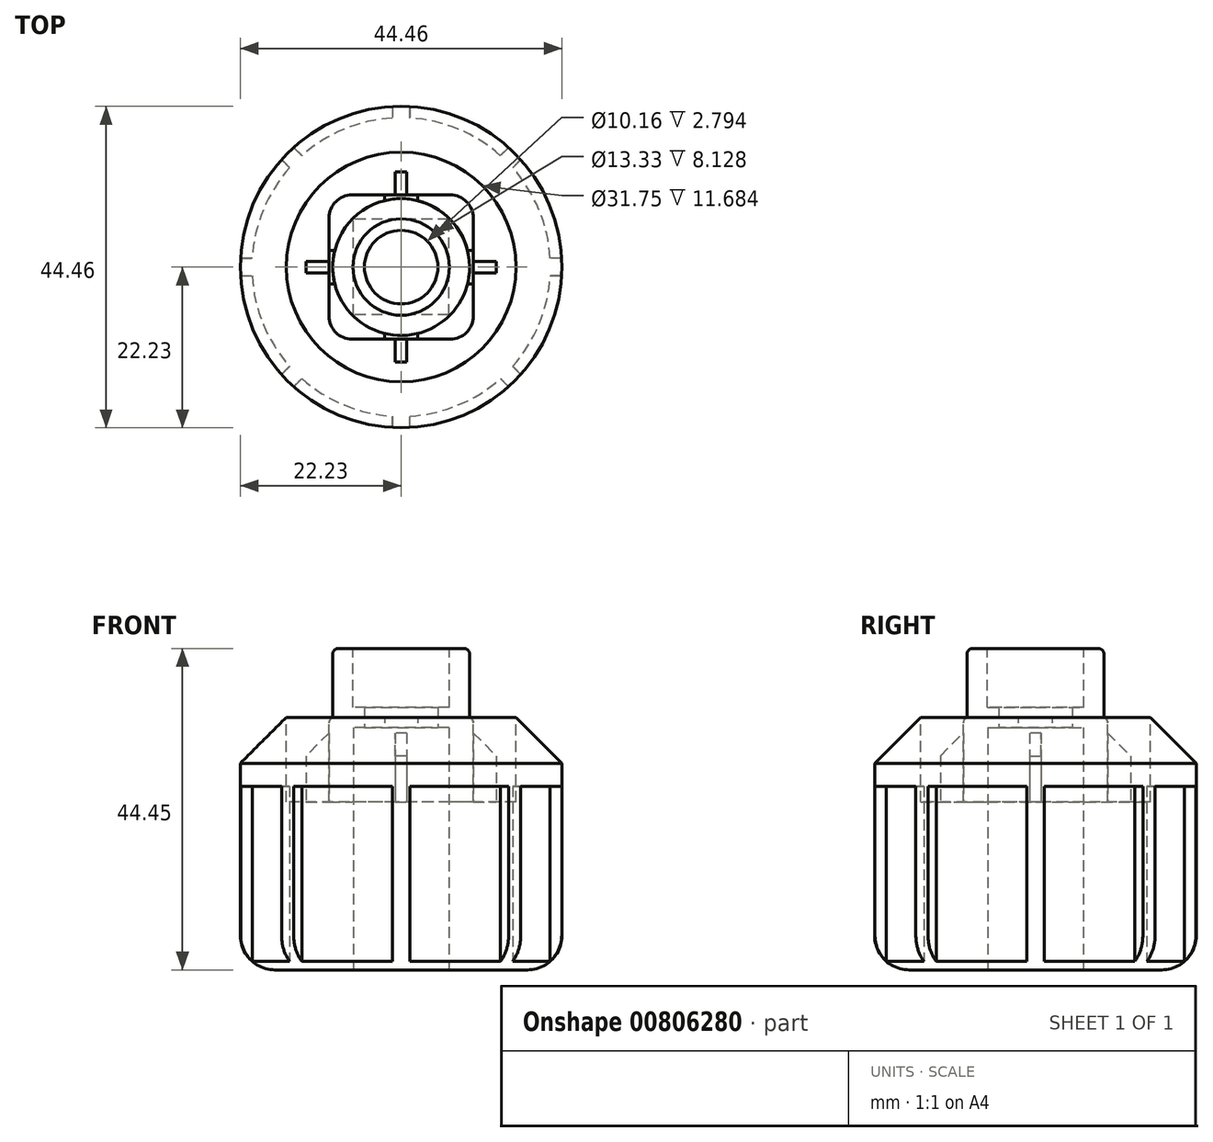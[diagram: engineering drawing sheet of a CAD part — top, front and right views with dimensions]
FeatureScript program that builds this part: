
annotation { "Feature Type Name" : "Feature", "Feature Type Description" : "" }
export const myFeature = defineFeature(function(context is Context, id is Id, definition is map)
    precondition{}
    {
        {
            var Q0;
            Q0=qCreatedBy(makeId("Top.planeOp"),FACE);
            var sketch = newSketch(context, id + "F0", { "sketchPlane" : qUnion([Q0])});
            skCircle(sketch, "E0", {"center": v(0, 0) * mm, "radius": 9.46 * mm});
            skCircle(sketch, "E1", {"center": v(0, 0) * mm, "radius": 5.08 * mm});
            skSolve(sketch);
        }
        {
            var Q0;
            Q0 = qSketchRegion(id + "F0", true);
            extrude(context, id + "F1", {"entities" : qUnion([Q0]), "depth" : 44.45 * mm, "offsetDistance" : 25.4 * mm});
        }
        {
            var Q0;
            Q0=makeQuery(id+"F1.opExtrude","CAP_FACE",FACE,{"disambiguationData":[OSD([sQuery(id+"F0.wireOp",EDGE,"E0"),sQuery(id+"F0.wireOp",EDGE,"E1")])],"isStart":true});
            var sketch = newSketch(context, id + "F2", { "sketchPlane" : qUnion([Q0])});
            skCircle(sketch, "E2", {"center": v(0, 0) * mm, "radius": 22.23 * mm});
            skCircle(sketch, "E3", {"center": v(0, 0) * mm, "radius": 5.08 * mm});
            skSolve(sketch);
        }
        {
            var Q0;
            Q0 = qSketchRegion(id + "F2", true);
            extrude(context, id + "F3", {"entities" : qUnion([Q0]), "operationType" : NewBodyOperationType.ADD, "oppositeDirection" : true, "depth" : 34.92 * mm, "offsetDistance" : 25.4 * mm});
        }
        {
            var Q0;
            Q0=makeQuery(id+"F1.opExtrude","CAP_FACE",FACE,{"disambiguationData":[OSD([sQuery(id+"F0.wireOp",EDGE,"E0"),sQuery(id+"F0.wireOp",EDGE,"E1")])],"isStart":false});
            var sketch = newSketch(context, id + "F4", { "sketchPlane" : qUnion([Q0])});
            skCircle(sketch, "E4", {"center": v(0, 0) * mm, "radius": 6.67 * mm});
            skSolve(sketch);
        }
        {
            var Q0;
            Q0 = qSketchRegion(id + "F4", true);
            extrude(context, id + "F5", {"entities" : qUnion([Q0]), "operationType" : NewBodyOperationType.REMOVE, "oppositeDirection" : true, "depth" : 8.13 * mm, "offsetDistance" : 25.4 * mm});
        }
        {
            var Q0;
            Q0=makeQuery(id+"F3.boolean.opBoolean","MERGE",FACE,{"derivedFrom":[makeQuery(id+"F1.opExtrude","CAP_FACE",FACE,{"disambiguationData":[OSD([sQuery(id+"F0.wireOp",EDGE,"E0"),sQuery(id+"F0.wireOp",EDGE,"E1")])],"isStart":true}),makeQuery(id+"F3.opExtrude","CAP_FACE",FACE,{"disambiguationData":[OSD([sQuery(id+"F2.wireOp",EDGE,"E2"),sQuery(id+"F2.wireOp",EDGE,"E3")])],"isStart":true})]});
            var sketch = newSketch(context, id + "F6", { "sketchPlane" : qUnion([Q0])});
            skLineSegment(sketch, "E5.bottom", {"start": v(6.6, 6.6) * mm, "end": v(-6.6, 6.6) * mm});
            skLineSegment(sketch, "E5.top", {"start": v(6.6, -6.6) * mm, "end": v(-6.6, -6.6) * mm});
            skLineSegment(sketch, "E5.left", {"start": v(6.6, 6.6) * mm, "end": v(6.6, -6.6) * mm});
            skLineSegment(sketch, "E5.right", {"start": v(-6.6, 6.6) * mm, "end": v(-6.6, -6.6) * mm});
            skPoint(sketch, "E5.middle", {"position": v(0, 0) * mm});
            skSolve(sketch);
        }
        {
            var Q0;
            Q0 = qSketchRegion(id + "F6", true);
            var Q1;
            Q1=makeQuery(id+"F1.opExtrude","CAP_FACE",FACE,{"disambiguationData":[OSD([sQuery(id+"F0.wireOp",EDGE,"E0"),sQuery(id+"F0.wireOp",EDGE,"E1")])],"isStart":false});
            extrude(context, id + "F7", {"entities" : qUnion([Q0, Q1]), "operationType" : NewBodyOperationType.REMOVE, "oppositeDirection" : true, "depth" : 33.53 * mm, "offsetDistance" : 25.4 * mm});
        }
        {
            var Q0;
            Q0=makeQuery(id+"F3.opExtrude","CAP_FACE",FACE,{"disambiguationData":[OSD([sQuery(id+"F2.wireOp",EDGE,"E2"),sQuery(id+"F2.wireOp",EDGE,"E3")])],"isStart":false});
            var sketch = newSketch(context, id + "F8", { "sketchPlane" : qUnion([Q0])});
            skLineSegment(sketch, "E6.bottom", {"start": v(6.8, 9.97) * mm, "end": v(-6.8, 9.97) * mm});
            skLineSegment(sketch, "E6.top", {"start": v(6.8, -9.97) * mm, "end": v(-6.8, -9.97) * mm});
            skLineSegment(sketch, "E6.left", {"start": v(9.97, 6.8) * mm, "end": v(9.97, -6.8) * mm});
            skLineSegment(sketch, "E6.right", {"start": v(-9.97, 6.8) * mm, "end": v(-9.97, -6.8) * mm});
            skPoint(sketch, "E6.middle", {"position": v(0, 0) * mm});
            skCircle(sketch, "E7", {"center": v(0, 0) * mm, "radius": 15.88 * mm});
            skPoint(sketch, "E8.visualSharp", {"position": v(-9.97, 9.97) * mm});
            skArc(sketch, "E8.filletArc", {"start": v(-6.8, 9.97) * mm, "mid": v(-9.04, 9.04) * mm, "end": v(-9.97, 6.8) * mm});
            skPoint(sketch, "E9.visualSharp", {"position": v(9.97, 9.97) * mm});
            skArc(sketch, "E9.filletArc", {"start": v(9.97, 6.8) * mm, "mid": v(9.04, 9.04) * mm, "end": v(6.8, 9.97) * mm});
            skPoint(sketch, "E10.visualSharp", {"position": v(9.97, -9.97) * mm});
            skArc(sketch, "E10.filletArc", {"start": v(6.8, -9.97) * mm, "mid": v(9.04, -9.04) * mm, "end": v(9.97, -6.8) * mm});
            skPoint(sketch, "E11.visualSharp", {"position": v(-9.97, -9.97) * mm});
            skArc(sketch, "E11.filletArc", {"start": v(-9.97, -6.8) * mm, "mid": v(-9.04, -9.04) * mm, "end": v(-6.8, -9.97) * mm});
            skSolve(sketch);
        }
        {
            var Q0;
            Q0 = qSketchRegion(id + "F8", true);
            extrude(context, id + "F9", {"entities" : qUnion([Q0]), "operationType" : NewBodyOperationType.REMOVE, "oppositeDirection" : true, "depth" : 11.68 * mm, "offsetDistance" : 25.4 * mm});
        }
        {
            var Q0;
            Q0=makeQuery(id+"F9.boolean.opBoolean","COPY",FACE,{"derivedFrom":makeQuery(id+"F9.opExtrude","CAP_FACE",FACE,{"disambiguationData":[OSD([sQuery(id+"F8.wireOp",EDGE,"E6.bottom"),sQuery(id+"F8.wireOp",EDGE,"E6.top"),sQuery(id+"F8.wireOp",EDGE,"E6.left"),sQuery(id+"F8.wireOp",EDGE,"E6.right"),sQuery(id+"F8.wireOp",EDGE,"E7"),sQuery(id+"F8.wireOp",EDGE,"E8.filletArc"),sQuery(id+"F8.wireOp",EDGE,"E9.filletArc"),sQuery(id+"F8.wireOp",EDGE,"E10.filletArc"),sQuery(id+"F8.wireOp",EDGE,"E11.filletArc")])],"isStart":false})});
            var sketch = newSketch(context, id + "F10", { "sketchPlane" : qUnion([Q0])});
            skLineSegment(sketch, "E12", {"start": v(-0.8, -9.97) * mm, "end": v(-0.8, -13.14) * mm});
            skLineSegment(sketch, "E13", {"start": v(-0.8, -13.14) * mm, "end": v(0.8, -13.14) * mm});
            skLineSegment(sketch, "E14", {"start": v(0.8, -13.14) * mm, "end": v(0.8, -9.97) * mm});
            skLineSegment(sketch, "E15", {"start": v(0.8, -9.97) * mm, "end": v(-0.8, -9.97) * mm});
            skLineSegment(sketch, "E16", {"start": v(0, -13.14) * mm, "end": v(0, -9.97) * mm, "construction": true});
            skLineSegment(sketch, "E17.1.0", {"start": v(-13.14, -0.8) * mm, "end": v(-9.97, -0.8) * mm});
            skLineSegment(sketch, "E17.1.1", {"start": v(-13.14, 0.8) * mm, "end": v(-13.14, -0.8) * mm});
            skLineSegment(sketch, "E17.1.2", {"start": v(-9.97, 0.8) * mm, "end": v(-13.14, 0.8) * mm});
            skLineSegment(sketch, "E17.1.3", {"start": v(-9.97, -0.8) * mm, "end": v(-9.97, 0.8) * mm});
            skLineSegment(sketch, "E17.2.0", {"start": v(-0.8, 13.14) * mm, "end": v(-0.8, 9.97) * mm});
            skLineSegment(sketch, "E17.2.1", {"start": v(0.8, 13.14) * mm, "end": v(-0.8, 13.14) * mm});
            skLineSegment(sketch, "E17.2.2", {"start": v(0.8, 9.97) * mm, "end": v(0.8, 13.14) * mm});
            skLineSegment(sketch, "E17.2.3", {"start": v(-0.8, 9.97) * mm, "end": v(0.8, 9.97) * mm});
            skLineSegment(sketch, "E17.3.0", {"start": v(13.14, 0.8) * mm, "end": v(9.97, 0.8) * mm});
            skLineSegment(sketch, "E17.3.1", {"start": v(13.14, -0.8) * mm, "end": v(13.14, 0.8) * mm});
            skLineSegment(sketch, "E17.3.2", {"start": v(9.97, -0.8) * mm, "end": v(13.14, -0.8) * mm});
            skLineSegment(sketch, "E17.3.3", {"start": v(9.97, 0.8) * mm, "end": v(9.97, -0.8) * mm});
            skPoint(sketch, "E17.center", {"position": v(0, 0) * mm});
            skLineSegment(sketch, "E17.anchor1", {"start": v(0, 0) * mm, "end": v(0.8, -13.14) * mm, "construction": true});
            skLineSegment(sketch, "E17.anchor2", {"start": v(0, 0) * mm, "end": v(13.14, 0.8) * mm, "construction": true});
            skSolve(sketch);
        }
        {
            var Q0;
            Q0=makeQuery(id+"F10.imprint","IMPRINT",FACE,{"disambiguationData":[TD([[makeQuery(id+"F10.imprint","IMPRINT",EDGE,{"derivedFrom":sQuery(id+"F10.wireOp",EDGE,"E17.1.0")}),1.0]])]});
            var Q1;
            Q1=makeQuery(id+"F10.imprint","IMPRINT",FACE,{"disambiguationData":[TD([[makeQuery(id+"F10.imprint","IMPRINT",EDGE,{"derivedFrom":sQuery(id+"F10.wireOp",EDGE,"E12")}),1.0]])]});
            var Q2;
            Q2=makeQuery(id+"F10.imprint","IMPRINT",FACE,{"disambiguationData":[TD([[makeQuery(id+"F10.imprint","IMPRINT",EDGE,{"derivedFrom":sQuery(id+"F10.wireOp",EDGE,"E17.3.0")}),1.0]])]});
            var Q3;
            Q3=makeQuery(id+"F10.imprint","IMPRINT",FACE,{"disambiguationData":[TD([[makeQuery(id+"F10.imprint","IMPRINT",EDGE,{"derivedFrom":sQuery(id+"F10.wireOp",EDGE,"E17.2.0")}),1.0]])]});
            var Q4;
            Q4 = qConstructionFilter(qBodyType(qCreatedBy(id + "F10" ,EDGE), BodyType.WIRE), ConstructionObject.NO);
            extrude(context, id + "F11", {"entities" : qUnion([Q0, Q1, Q2, Q3]), "operationType" : NewBodyOperationType.ADD, "surfaceEntities" : qUnion([Q4]), "depth" : 9.52 * mm, "offsetDistance" : 25.4 * mm});
        }
        {
            var Q0;
            Q0=makeQuery(id+"F11.opExtrude","CAP_EDGE",EDGE,{"disambiguationData":[OSD([sQuery(id+"F10.wireOp",EDGE,"E17.1.1")])],"isStart":false});
            var Q1;
            Q1=makeQuery(id+"F11.opExtrude","CAP_EDGE",EDGE,{"disambiguationData":[OSD([sQuery(id+"F10.wireOp",EDGE,"E13")])],"isStart":false});
            var Q2;
            Q2=makeQuery(id+"F11.opExtrude","CAP_EDGE",EDGE,{"disambiguationData":[OSD([sQuery(id+"F10.wireOp",EDGE,"E17.3.1")])],"isStart":false});
            var Q3;
            Q3=makeQuery(id+"F11.opExtrude","CAP_EDGE",EDGE,{"disambiguationData":[OSD([sQuery(id+"F10.wireOp",EDGE,"E17.2.1")])],"isStart":false});
            chamfer(context, id + "F12", {"entities" : qUnion([Q0, Q1, Q2, Q3]), "width" : 3.17 * mm, "tangentPropagation" : true});
        }
        {
            var Q0;
            Q0=makeQuery(id+"F3.boolean.opBoolean","MERGE",FACE,{"derivedFrom":[makeQuery(id+"F1.opExtrude","CAP_FACE",FACE,{"disambiguationData":[OSD([sQuery(id+"F0.wireOp",EDGE,"E0"),sQuery(id+"F0.wireOp",EDGE,"E1")])],"isStart":true}),makeQuery(id+"F3.opExtrude","CAP_FACE",FACE,{"disambiguationData":[OSD([sQuery(id+"F2.wireOp",EDGE,"E2"),sQuery(id+"F2.wireOp",EDGE,"E3")])],"isStart":true})]});
            var sketch = newSketch(context, id + "F13", { "sketchPlane" : qUnion([Q0])});
            skCircle(sketch, "E18", {"center": v(0, 0) * mm, "radius": 20.64 * mm});
            skCircle(sketch, "E19", {"center": v(0, 0) * mm, "radius": 22.23 * mm});
            skLineSegment(sketch, "E20", {"start": v(22.23, 0) * mm, "end": v(-22.23, 0) * mm, "construction": true});
            skLineSegment(sketch, "E21", {"start": v(22.2, -1.2) * mm, "end": v(20.6, -1.2) * mm});
            skLineSegment(sketch, "E22", {"start": v(22.2, 1.2) * mm, "end": v(20.6, 1.2) * mm});
            skLineSegment(sketch, "E23.1.0", {"start": v(16.53, 14.85) * mm, "end": v(15.41, 13.73) * mm});
            skLineSegment(sketch, "E23.1.1", {"start": v(14.85, 16.53) * mm, "end": v(13.73, 15.41) * mm});
            skLineSegment(sketch, "E23.2.0", {"start": v(1.2, 22.2) * mm, "end": v(1.2, 20.6) * mm});
            skLineSegment(sketch, "E23.2.1", {"start": v(-1.2, 22.2) * mm, "end": v(-1.2, 20.6) * mm});
            skLineSegment(sketch, "E23.3.0", {"start": v(-14.85, 16.53) * mm, "end": v(-13.73, 15.41) * mm});
            skLineSegment(sketch, "E23.3.1", {"start": v(-16.53, 14.85) * mm, "end": v(-15.41, 13.73) * mm});
            skLineSegment(sketch, "E23.4.0", {"start": v(-22.2, 1.2) * mm, "end": v(-20.6, 1.2) * mm});
            skLineSegment(sketch, "E23.4.1", {"start": v(-22.2, -1.2) * mm, "end": v(-20.6, -1.2) * mm});
            skLineSegment(sketch, "E23.5.0", {"start": v(-16.53, -14.85) * mm, "end": v(-15.41, -13.73) * mm});
            skLineSegment(sketch, "E23.5.1", {"start": v(-14.85, -16.53) * mm, "end": v(-13.73, -15.41) * mm});
            skLineSegment(sketch, "E23.6.0", {"start": v(-1.2, -22.2) * mm, "end": v(-1.2, -20.6) * mm});
            skLineSegment(sketch, "E23.6.1", {"start": v(1.2, -22.2) * mm, "end": v(1.2, -20.6) * mm});
            skLineSegment(sketch, "E23.7.0", {"start": v(14.85, -16.53) * mm, "end": v(13.73, -15.41) * mm});
            skLineSegment(sketch, "E23.7.1", {"start": v(16.53, -14.85) * mm, "end": v(15.41, -13.73) * mm});
            skSolve(sketch);
        }
        {
            var Q0;
            {var subQ0=sQuery(id+"F13.wireOp",EDGE,"E21");Q0=makeQuery(id+"F13.imprint","IMPRINT",FACE,{"disambiguationData":[TD([[makeQuery(id+"F13.imprint","IMPRINT",EDGE,{"derivedFrom":subQ0}),1.0]])]});}
            var Q1;
            {var subQ0=sQuery(id+"F13.wireOp",EDGE,"E23.6.1");Q1=makeQuery(id+"F13.imprint","IMPRINT",FACE,{"disambiguationData":[TD([[makeQuery(id+"F13.imprint","IMPRINT",EDGE,{"derivedFrom":subQ0}),-1.0]])]});}
            var Q2;
            {var subQ0=sQuery(id+"F13.wireOp",EDGE,"E23.5.1");Q2=makeQuery(id+"F13.imprint","IMPRINT",FACE,{"disambiguationData":[TD([[makeQuery(id+"F13.imprint","IMPRINT",EDGE,{"derivedFrom":subQ0}),-1.0]])]});}
            var Q3;
            {var subQ0=sQuery(id+"F13.wireOp",EDGE,"E23.4.1");Q3=makeQuery(id+"F13.imprint","IMPRINT",FACE,{"disambiguationData":[TD([[makeQuery(id+"F13.imprint","IMPRINT",EDGE,{"derivedFrom":subQ0}),-1.0]])]});}
            var Q4;
            {var subQ0=sQuery(id+"F13.wireOp",EDGE,"E23.3.1");Q4=makeQuery(id+"F13.imprint","IMPRINT",FACE,{"disambiguationData":[TD([[makeQuery(id+"F13.imprint","IMPRINT",EDGE,{"derivedFrom":subQ0}),-1.0]])]});}
            var Q5;
            {var subQ0=sQuery(id+"F13.wireOp",EDGE,"E23.2.1");Q5=makeQuery(id+"F13.imprint","IMPRINT",FACE,{"disambiguationData":[TD([[makeQuery(id+"F13.imprint","IMPRINT",EDGE,{"derivedFrom":subQ0}),-1.0]])]});}
            var Q6;
            {var subQ0=sQuery(id+"F13.wireOp",EDGE,"E23.1.1");Q6=makeQuery(id+"F13.imprint","IMPRINT",FACE,{"disambiguationData":[TD([[makeQuery(id+"F13.imprint","IMPRINT",EDGE,{"derivedFrom":subQ0}),-1.0]])]});}
            var Q7;
            {var subQ0=sQuery(id+"F13.wireOp",EDGE,"E22");Q7=makeQuery(id+"F13.imprint","IMPRINT",FACE,{"disambiguationData":[TD([[makeQuery(id+"F13.imprint","IMPRINT",EDGE,{"derivedFrom":subQ0}),-1.0]])]});}
            extrude(context, id + "F14", {"entities" : qUnion([Q0, Q1, Q2, Q3, Q4, Q5, Q6, Q7]), "operationType" : NewBodyOperationType.REMOVE, "oppositeDirection" : true, "depth" : 25.4 * mm, "offsetDistance" : 25.4 * mm});
        }
        {
            var Q0;
            {var subQ0=sQuery(id+"F2.wireOp",EDGE,"E2");Q0=makeQuery(id+"F14.boolean.opBoolean","SPLIT",EDGE,{"disambiguationData":[TD([makeQuery(id+"F14.opExtrude","SWEPT_FACE",FACE,{"disambiguationData":[OSD([sQuery(id+"F13.wireOp",EDGE,"E21")])]})])],"derivedFrom":makeQuery(id+"F3.opExtrude","CAP_EDGE",EDGE,{"disambiguationData":[OSD([subQ0])],"isStart":true})});}
            fillet(context, id + "F15", {"entities" : qUnion([Q0]), "radius" : 4.76 * mm, "tangentPropagation" : true, "allowEdgeOverflow" : false});
        }
        {
            var Q0;
            Q0=makeQuery(id+"F3.opExtrude","CAP_EDGE",EDGE,{"disambiguationData":[OSD([sQuery(id+"F2.wireOp",EDGE,"E2")])],"isStart":false});
            chamfer(context, id + "F16", {"entities" : qUnion([Q0]), "width" : 6.35 * mm, "tangentPropagation" : true});
        }
        {
            var Q0;
            Q0=makeQuery(id+"F9.boolean.opBoolean","COPY",EDGE,{"derivedFrom":makeQuery(id+"F9.opExtrude","CAP_EDGE",EDGE,{"disambiguationData":[OSD([sQuery(id+"F8.wireOp",EDGE,"E6.bottom")])],"isStart":true})});
            var Q1;
            Q1=makeQuery(id+"F1.opExtrude","CAP_EDGE",EDGE,{"disambiguationData":[OSD([sQuery(id+"F0.wireOp",EDGE,"E0")])],"isStart":false});
            var Q2;
            Q2=makeQuery(id+"F5.boolean.opBoolean","COPY",EDGE,{"derivedFrom":makeQuery(id+"F5.opExtrude","CAP_EDGE",EDGE,{"disambiguationData":[OSD([sQuery(id+"F4.wireOp",EDGE,"E4")])],"isStart":true})});
            fillet(context, id + "F17", {"entities" : qUnion([Q0, Q1, Q2]), "radius" : 0.8 * mm, "tangentPropagation" : true, "allowEdgeOverflow" : false});
        }
    });
